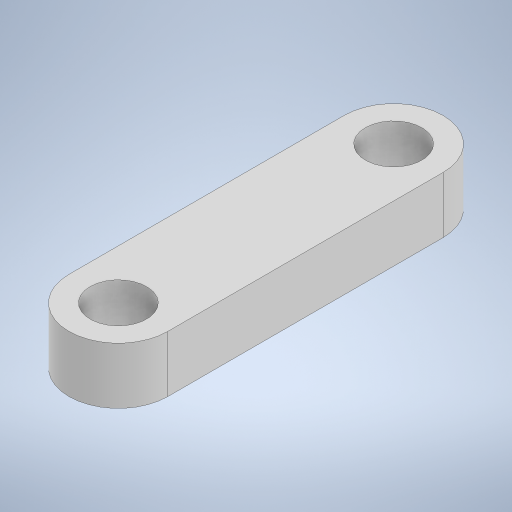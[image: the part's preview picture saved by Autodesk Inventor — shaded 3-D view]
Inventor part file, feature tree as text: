
AUTODESK INVENTOR PART (.ipt)
format: ipt  version: 2023.2 (Build 272271030, 271C)  size: 226,304 bytes
history: native  units: mm
features: extrude x1, sketch x1
ambient origin geometry x8: Origin, YZ Plane, XZ Plane, XY Plane, X Axis, Y Axis, Z Axis, Center Point
bodies: Solid1 (feature_tree)
feature tree (2):
  extrude  "Extrusion1"  Depth=7.0mm
  sketch  "Sketch1"  dims[d0=7.0mm d1=7.0mm d2=19.5mm d3=19.5mm d6=14.0mm d7=14.0mm d8=8.0mm d9=8.0mm d10=14.0mm d13=14.0mm d14=39.0mm d15=53.0mm d16=8.0mm d17=0.0mm]
